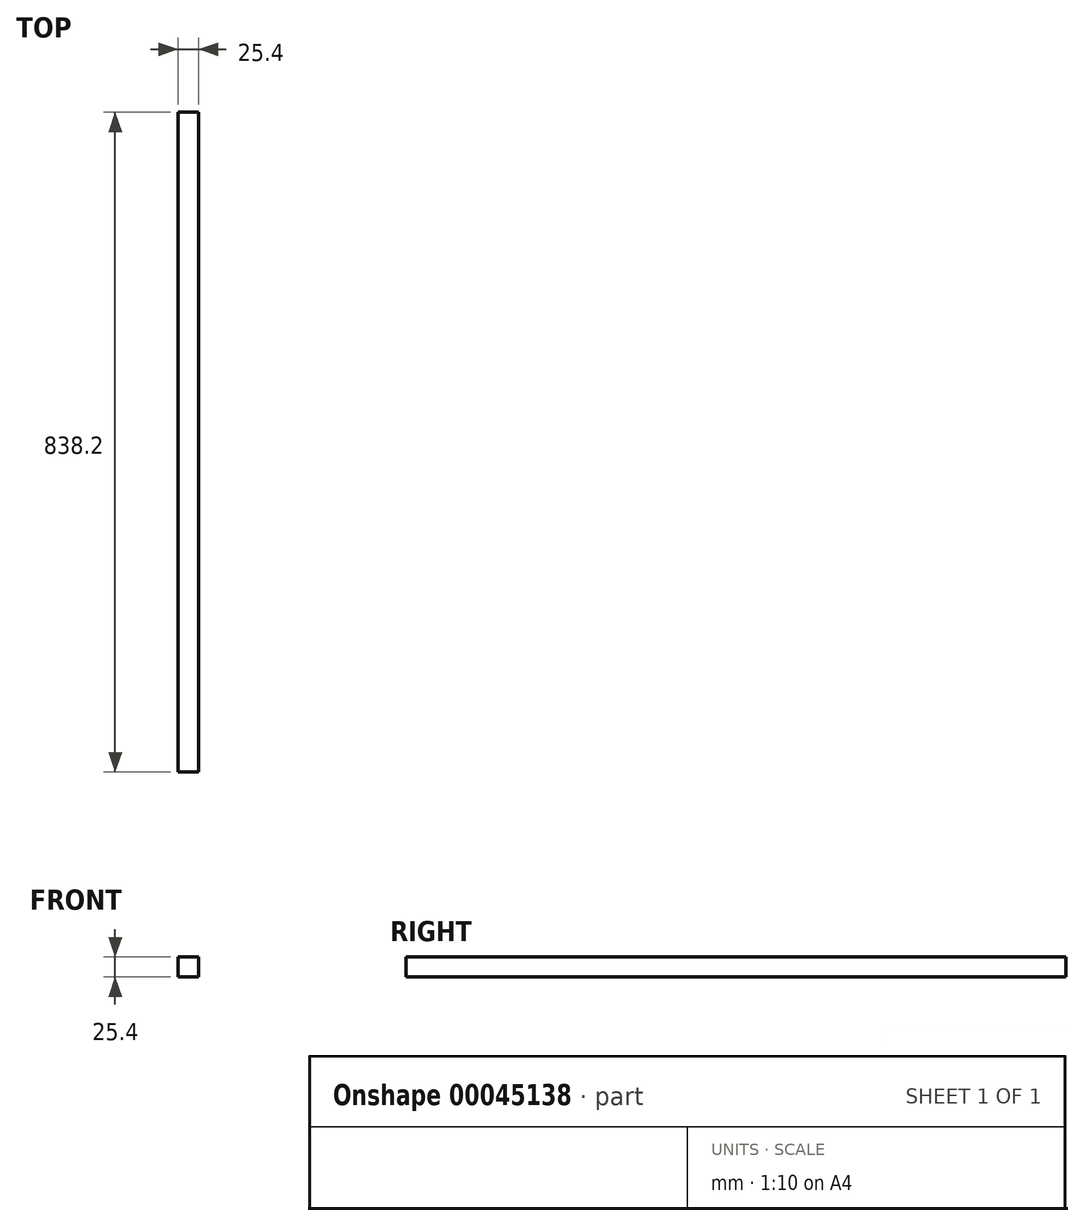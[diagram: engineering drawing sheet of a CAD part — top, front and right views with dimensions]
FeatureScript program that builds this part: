
annotation { "Feature Type Name" : "Feature", "Feature Type Description" : "" }
export const myFeature = defineFeature(function(context is Context, id is Id, definition is map)
    precondition{}
    {
        {
            var Q0;
            Q0=qCreatedBy(makeId("Front.planeOp"),FACE);
            var sketch = newSketch(context, id + "F0", { "sketchPlane" : qUnion([Q0])});
            skLineSegment(sketch, "E0.rect.bottom", {"start": v(12.7, -12.7) * mm, "end": v(-12.7, -12.7) * mm});
            skLineSegment(sketch, "E0.rect.top", {"start": v(12.7, 12.7) * mm, "end": v(-12.7, 12.7) * mm});
            skLineSegment(sketch, "E0.rect.left", {"start": v(12.7, -12.7) * mm, "end": v(12.7, 12.7) * mm});
            skLineSegment(sketch, "E0.rect.right", {"start": v(-12.7, -12.7) * mm, "end": v(-12.7, 12.7) * mm});
            skPoint(sketch, "E0.rect.middle", {"position": v(0, 0) * mm});
            skSolve(sketch);
        }
        {
            var Q0;
            Q0=makeQuery(id+"F0.imprint","IMPRINT",FACE,{"disambiguationData":[TD([[makeQuery(id+"F0.imprint","IMPRINT",EDGE,{"derivedFrom":sQuery(id+"F0.wireOp",EDGE,"E0.rect.bottom")}),-1.0]])]});
            extrude(context, id + "F1", {"entities" : qUnion([Q0]), "depth" : 838.2 * mm});
        }
    });
